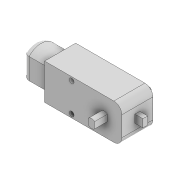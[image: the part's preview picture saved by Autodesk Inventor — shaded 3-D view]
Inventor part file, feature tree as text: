
AUTODESK INVENTOR PART (.ipt)
format: ipt  version: 2022 (Build 260153000, 153)  size: 164,864 bytes
history: native  units: mm
features: sketch x5, extrude x4, fillet x2, mirror x1, hole x1, projected_geometry x1
ambient origin geometry x8: Origin, YZ Plane, XZ Plane, XY Plane, X Axis, Y Axis, Z Axis, Center Point
bodies: Solid1 (feature_tree)
feature tree (14):
  extrude  "Extrusion1"  Depth=48.5mm
  extrude  "Extrusion2"  Depth=3.0mm
  fillet  "Fillet1"  Radius=5.0mm
  extrude  "Extrusion3"  Depth=5.0mm
  fillet  "Fillet2"  Radius=20.0mm
  extrude  "Extrusion4"  Depth=16.0mm TaperAngle=0.0deg
  mirror  "Mirror1"
  hole  "Hole1"  [1 undecoded]
  sketch  "Sketch1"  dims[d0=19.5mm d1=48.5mm]
  sketch  "Sketch2"  dims[d2=22.5mm d3=0.0mm d4=3.0mm d5=5.0mm]
  sketch  "Sketch3"  dims[d6=5.0mm d7=0.0mm d8=5.0mm d9=20.0mm]
  sketch  "Sketch4"  dims[d10=15.0mm d11=16.0mm d12=0.0mm]
  sketch  "Sketch5"  dims[d13=4.0mm d14=5.5mm d15=4.0mm d16=11.25mm d17=11.0mm d18=8.0mm d19=0.0mm d21=18.0mm d22=17.0mm d23=3.0mm d24=6.0mm d25=6.3mm d26=2.0mm d27=90.0deg d28=8.0mm d29=20.594885mm]
  projected_geometry  "Project Cut Edges1"
note: 1 required parameter value undecoded (feature->parameter linkage not recoverable at this tier; creation-order binding heuristic only, values carry confidence <= 0.55)
